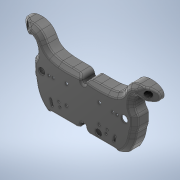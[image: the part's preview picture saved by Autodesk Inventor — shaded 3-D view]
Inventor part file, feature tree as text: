
AUTODESK INVENTOR PART (.ipt)
format: ipt  version: 2020 (Build 240168000, 168)  size: 5,510,656 bytes
history: native  units: mm
features: reference x15, extrude x9, sketch x9, other x5, chamfer x4, plane x3, fillet x2, mirror x2, shell x1
ambient origin geometry x8: Origin, YZ Plane, XZ Plane, XY Plane, X Axis, Y Axis, Z Axis, Center Point
bodies: Volumenkörper1 (feature_tree)
feature tree (50):
  plane  "Arbeitsebene1"
  extrude  "Extrusion1"  Depth=6.108652mm
  plane  "Arbeitsebene2"
  chamfer  "Fase1"  Distance=40.0mm
  extrude  "Extrusion2"  Depth=3.0mm
  fillet  "Rundung1"  Radius=2.5mm
  fillet  "Rundung3"  Radius=1.0mm
  shell  "Wandung1"  Thickness=0.5mm
  other  "Verdickung1"
  extrude  "Extrusion4"  Depth=2.0mm
  extrude  "Extrusion5"  Depth=8.0mm
  extrude  "Extrusion6"  Depth=10.0mm TaperAngle=0.0deg
  extrude  "Extrusion7"  Depth=10.0mm
  extrude  "Extrusion8"  Depth=10.0mm
  mirror  "Spiegeln1"
  plane  "Arbeitsebene5"
  extrude  "Extrusion9"  Depth=10.0mm
  chamfer  "Fase3"  Distance=2.626001mm
  chamfer  "Fase4"  Distance=55.0mm
  chamfer  "Fase2"  Distance=10.0mm
  sketch  "Skizze10"  dims[d28=55.0mm d29=2.626001mm d30=4.091407mm d31=2.626001mm d33=55.0mm d34=10.0mm d35=0.0mm d36=12.0mm d37=13.6mm d38=12.0mm d39=13.6mm d40=10.0mm d41=0.0mm d42=6.0mm d43=10.8mm d44=6.0mm d45=2.0mm d46=10.0mm d47=0.0mm d48=-5.0mm d49=0.978468mm d51=0.489234mm d52=172.63874mm d53=15.0mm d54=4.0mm d55=33.0mm d56=10.0mm d57=0.0mm d58=1.0mm d59=2.0mm d60=45.0deg d61=18.5mm d62=2.0mm d63=6.457718mm d64=0.872665mm d65=3.5mm d66=0.8mm d67=18.5mm d68=2.0mm d69=6.283185mm d70=13.5mm d71=1.0mm d72=0.0mm]
  extrude  "Extrusion10"  Depth=10.0mm
  mirror  "Spiegeln2"
  sketch  "Skizze1"  dims[d0=23.0mm d1=0.0mm d2=6.108652mm]
  reference  "Referenz1"
  reference  "Referenz2"
  reference  "Referenz3"
  reference  "Referenz4"
  reference  "Referenz5"
  sketch  "Skizze2"  dims[d3=6.108652mm]
  sketch  "Skizze4"  dims[d4=17.0mm d5=40.0mm d6=0.0mm]
  reference  "Referenz6"
  reference  "Referenz7"
  reference  "Referenz8"
  reference  "Referenz9"
  reference  "Referenz10"
  reference  "Referenz11"
  reference  "Referenz12"
  reference  "Referenz13"
  reference  "Referenz14"
  reference  "Referenz15"
  sketch  "Skizze5"  dims[d9=5.5mm d10=2.0mm d11=45.0deg d12=3.0mm d13=2.5mm d15=1.0mm d16=0.5mm d17=0.5mm]
  sketch  "Skizze6"  dims[d18=23.0mm d19=0.0mm d20=2.0mm]
  sketch  "Skizze7"  dims[d21=8.0mm d22=8.0mm]
  sketch  "Skizze8"  dims[d23=5.0mm d24=10.0mm d25=0.0mm]
  sketch  "Skizze9"  dims[d26=2.0mm d27=10.0mm]
  other  "08-01-00-000_TurnGTBarebone.iam"
  other  "08-02-01-002_PCBOutline:1"
  other  "Front Plate:1"
  other  "08-02-01-005_pcbDummyFunkySwitch:1"
